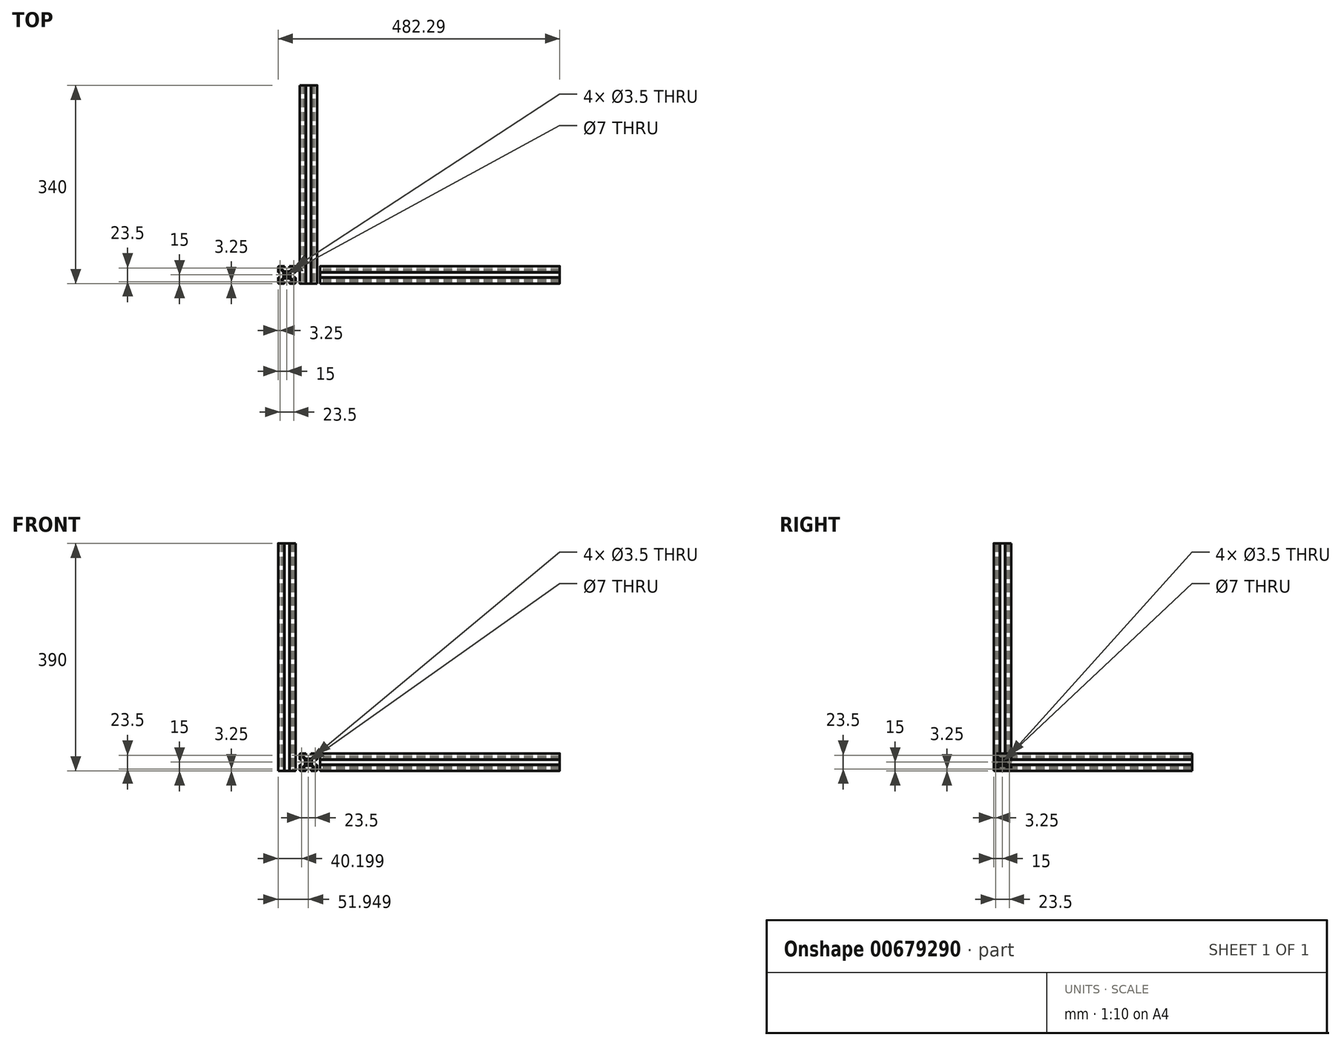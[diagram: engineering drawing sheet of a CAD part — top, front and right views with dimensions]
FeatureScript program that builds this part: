
annotation { "Feature Type Name" : "Feature", "Feature Type Description" : "" }
export const myFeature = defineFeature(function(context is Context, id is Id, definition is map)
    precondition{}
    {
        {
            var Q0;
            Q0=qCreatedBy(makeId("Front.planeOp"),FACE);
            var sketch = newSketch(context, id + "F0", { "sketchPlane" : qUnion([Q0])});
            skLineSegment(sketch, "E0.bottom", {"start": v(-33.34, 30) * mm, "end": v(-25.04, 30) * mm});
            skLineSegment(sketch, "E0.top", {"start": v(-33.34, 0) * mm, "end": v(-25.04, 0) * mm});
            skLineSegment(sketch, "E0.left", {"start": v(-35.34, 28) * mm, "end": v(-35.34, 19.7) * mm});
            skLineSegment(sketch, "E0.right", {"start": v(-5.34, 28) * mm, "end": v(-5.34, 19.7) * mm});
            skPoint(sketch, "E1", {"position": v(-20.34, 15) * mm});
            skLineSegment(sketch, "E2.bottom", {"start": v(-28.84, 27.8) * mm, "end": v(-24.44, 27.8) * mm});
            skLineSegment(sketch, "E2.left", {"start": v(-33.14, 23.5) * mm, "end": v(-33.14, 19.1) * mm});
            skCircle(sketch, "E3", {"center": v(-20.34, 15) * mm, "radius": 3.5 * mm});
            skCircle(sketch, "E4", {"center": v(-32.1, 3.25) * mm, "radius": 1.75 * mm});
            skCircle(sketch, "E5", {"center": v(-32.1, 26.75) * mm, "radius": 1.75 * mm});
            skCircle(sketch, "E6", {"center": v(-8.6, 26.75) * mm, "radius": 1.75 * mm});
            skCircle(sketch, "E7", {"center": v(-8.6, 3.25) * mm, "radius": 1.75 * mm});
            skLineSegment(sketch, "E8.right", {"start": v(-16.24, 2.2) * mm, "end": v(-16.24, 0.5) * mm});
            skLineSegment(sketch, "E9.trimOffspring", {"start": v(-16.24, 2.2) * mm, "end": v(-11.84, 2.2) * mm});
            skLineSegment(sketch, "E10.trimOffspring", {"start": v(-15.64, 0) * mm, "end": v(-7.34, 0) * mm});
            skLineSegment(sketch, "E11.trimOffspring", {"start": v(-24.44, 2.2) * mm, "end": v(-24.44, 0.5) * mm});
            skLineSegment(sketch, "E12.trimOffspring", {"start": v(-28.84, 2.2) * mm, "end": v(-24.44, 2.2) * mm});
            skLineSegment(sketch, "E13.trimOffspring", {"start": v(-7.54, 23.5) * mm, "end": v(-7.54, 19.1) * mm});
            skLineSegment(sketch, "E14", {"start": v(-24.44, 27.8) * mm, "end": v(-24.44, 29.5) * mm});
            skLineSegment(sketch, "E15", {"start": v(-16.24, 27.8) * mm, "end": v(-16.24, 29.5) * mm});
            skLineSegment(sketch, "E16.trimOffspring", {"start": v(-15.64, 30) * mm, "end": v(-7.34, 30) * mm});
            skLineSegment(sketch, "E17.trimOffspring", {"start": v(-16.24, 27.8) * mm, "end": v(-11.84, 27.8) * mm});
            skLineSegment(sketch, "E18", {"start": v(-7.54, 10.9) * mm, "end": v(-5.84, 10.9) * mm});
            skLineSegment(sketch, "E19", {"start": v(-7.54, 19.1) * mm, "end": v(-5.84, 19.1) * mm});
            skLineSegment(sketch, "E20", {"start": v(-33.14, 10.9) * mm, "end": v(-34.84, 10.9) * mm});
            skLineSegment(sketch, "E21", {"start": v(-33.14, 19.1) * mm, "end": v(-34.84, 19.1) * mm});
            skLineSegment(sketch, "E22.trimOffspring", {"start": v(-5.34, 10.3) * mm, "end": v(-5.34, 2) * mm});
            skLineSegment(sketch, "E23.trimOffspring", {"start": v(-7.54, 10.9) * mm, "end": v(-7.54, 6.5) * mm});
            skLineSegment(sketch, "E24.trimOffspring", {"start": v(-33.14, 10.9) * mm, "end": v(-33.14, 6.5) * mm});
            skLineSegment(sketch, "E25.trimOffspring", {"start": v(-35.34, 10.3) * mm, "end": v(-35.34, 2) * mm});
            skLineSegment(sketch, "E26.bottom", {"start": v(-24.93, 21) * mm, "end": v(-15.75, 21) * mm});
            skLineSegment(sketch, "E26.top", {"start": v(-24.93, 9) * mm, "end": v(-15.75, 9) * mm});
            skLineSegment(sketch, "E26.left", {"start": v(-26.34, 19.59) * mm, "end": v(-26.34, 10.41) * mm});
            skLineSegment(sketch, "E26.right", {"start": v(-14.34, 19.59) * mm, "end": v(-14.34, 10.41) * mm});
            skLineSegment(sketch, "E27", {"start": v(-28.84, 27.8) * mm, "end": v(-28.84, 24.91) * mm});
            skLineSegment(sketch, "E28", {"start": v(-30.25, 23.5) * mm, "end": v(-33.14, 23.5) * mm});
            skLineSegment(sketch, "E29", {"start": v(-11.84, 24.91) * mm, "end": v(-11.84, 27.8) * mm});
            skLineSegment(sketch, "E30", {"start": v(-10.43, 23.5) * mm, "end": v(-7.54, 23.5) * mm});
            skLineSegment(sketch, "E31", {"start": v(-10.43, 6.5) * mm, "end": v(-7.54, 6.5) * mm});
            skLineSegment(sketch, "E32", {"start": v(-11.84, 5.09) * mm, "end": v(-11.84, 2.2) * mm});
            skLineSegment(sketch, "E33", {"start": v(-28.84, 5.09) * mm, "end": v(-28.84, 2.2) * mm});
            skLineSegment(sketch, "E34", {"start": v(-30.25, 6.5) * mm, "end": v(-33.14, 6.5) * mm});
            skLineSegment(sketch, "E35", {"start": v(-30.25, 23.5) * mm, "end": v(-26.34, 19.59) * mm});
            skLineSegment(sketch, "E36", {"start": v(-28.84, 24.91) * mm, "end": v(-24.93, 21) * mm});
            skLineSegment(sketch, "E37", {"start": v(-14.34, 10.41) * mm, "end": v(-10.43, 6.5) * mm});
            skLineSegment(sketch, "E38", {"start": v(-15.75, 9) * mm, "end": v(-11.84, 5.09) * mm});
            skLineSegment(sketch, "E39", {"start": v(-28.84, 5.09) * mm, "end": v(-24.93, 9) * mm});
            skLineSegment(sketch, "E40", {"start": v(-30.25, 6.5) * mm, "end": v(-26.34, 10.41) * mm});
            skLineSegment(sketch, "E41", {"start": v(-15.75, 21) * mm, "end": v(-11.84, 24.91) * mm});
            skLineSegment(sketch, "E42", {"start": v(-14.34, 19.59) * mm, "end": v(-10.43, 23.5) * mm});
            skArc(sketch, "E43.filletArc", {"start": v(-33.34, 30) * mm, "mid": v(-34.75, 29.41) * mm, "end": v(-35.34, 28) * mm});
            skArc(sketch, "E44.filletArc", {"start": v(-5.34, 28) * mm, "mid": v(-5.93, 29.41) * mm, "end": v(-7.34, 30) * mm});
            skArc(sketch, "E45.filletArc", {"start": v(-7.34, 0) * mm, "mid": v(-5.93, 0.59) * mm, "end": v(-5.34, 2) * mm});
            skArc(sketch, "E46.filletArc", {"start": v(-35.34, 2) * mm, "mid": v(-34.75, 0.59) * mm, "end": v(-33.34, 0) * mm});
            skLineSegment(sketch, "E47", {"start": v(-5.84, 19.1) * mm, "end": v(-5.84, 19.7) * mm});
            skLineSegment(sketch, "E48", {"start": v(-5.84, 19.7) * mm, "end": v(-5.34, 19.7) * mm});
            skLineSegment(sketch, "E49.top", {"start": v(-5.34, 10.3) * mm, "end": v(-5.84, 10.3) * mm});
            skLineSegment(sketch, "E49.right", {"start": v(-5.84, 10.9) * mm, "end": v(-5.84, 10.3) * mm});
            skLineSegment(sketch, "E50.top", {"start": v(-16.24, 0.5) * mm, "end": v(-15.64, 0.5) * mm});
            skLineSegment(sketch, "E50.right", {"start": v(-15.64, 0) * mm, "end": v(-15.64, 0.5) * mm});
            skLineSegment(sketch, "E51.top", {"start": v(-24.44, 0.5) * mm, "end": v(-25.04, 0.5) * mm});
            skLineSegment(sketch, "E51.right", {"start": v(-25.04, 0) * mm, "end": v(-25.04, 0.5) * mm});
            skLineSegment(sketch, "E52.top", {"start": v(-35.34, 10.3) * mm, "end": v(-34.84, 10.3) * mm});
            skLineSegment(sketch, "E52.right", {"start": v(-34.84, 10.9) * mm, "end": v(-34.84, 10.3) * mm});
            skLineSegment(sketch, "E53.top", {"start": v(-35.34, 19.7) * mm, "end": v(-34.84, 19.7) * mm});
            skLineSegment(sketch, "E53.right", {"start": v(-34.84, 19.1) * mm, "end": v(-34.84, 19.7) * mm});
            skLineSegment(sketch, "E54.top", {"start": v(-24.44, 29.5) * mm, "end": v(-25.04, 29.5) * mm});
            skLineSegment(sketch, "E54.right", {"start": v(-25.04, 30) * mm, "end": v(-25.04, 29.5) * mm});
            skLineSegment(sketch, "E55.top", {"start": v(-16.24, 29.5) * mm, "end": v(-15.64, 29.5) * mm});
            skLineSegment(sketch, "E55.right", {"start": v(-15.64, 30) * mm, "end": v(-15.64, 29.5) * mm});
            skSolve(sketch);
        }
        {
            var Q0;
            Q0=qSketchRegion(id+"F0",true);
            extrude(context, id + "F1", {"entities" : qUnion([Q0]), "oppositeDirection" : true, "depth" : 340 * mm, "offsetDistance" : 25 * mm});
        }
        {
            var Q0;
            Q0=qCreatedBy(makeId("Top.planeOp"),FACE);
            var sketch = newSketch(context, id + "F2", { "sketchPlane" : qUnion([Q0])});
            skLineSegment(sketch, "E56.bottom", {"start": v(-70.29, 30) * mm, "end": v(-61.99, 30) * mm});
            skLineSegment(sketch, "E56.top", {"start": v(-70.29, 0) * mm, "end": v(-61.99, 0) * mm});
            skLineSegment(sketch, "E56.left", {"start": v(-72.29, 28) * mm, "end": v(-72.29, 19.7) * mm});
            skLineSegment(sketch, "E56.right", {"start": v(-42.29, 28) * mm, "end": v(-42.29, 19.7) * mm});
            skPoint(sketch, "E57", {"position": v(-57.29, 15) * mm});
            skLineSegment(sketch, "E58.bottom", {"start": v(-65.79, 27.8) * mm, "end": v(-61.39, 27.8) * mm});
            skLineSegment(sketch, "E58.left", {"start": v(-70.09, 23.5) * mm, "end": v(-70.09, 19.1) * mm});
            skCircle(sketch, "E59", {"center": v(-57.29, 15) * mm, "radius": 3.5 * mm});
            skCircle(sketch, "E60", {"center": v(-69.04, 3.25) * mm, "radius": 1.75 * mm});
            skCircle(sketch, "E61", {"center": v(-69.04, 26.75) * mm, "radius": 1.75 * mm});
            skCircle(sketch, "E62", {"center": v(-45.54, 26.75) * mm, "radius": 1.75 * mm});
            skCircle(sketch, "E63", {"center": v(-45.54, 3.25) * mm, "radius": 1.75 * mm});
            skLineSegment(sketch, "E64.right", {"start": v(-53.19, 2.2) * mm, "end": v(-53.19, 0.5) * mm});
            skLineSegment(sketch, "E65.trimOffspring", {"start": v(-53.19, 2.2) * mm, "end": v(-48.79, 2.2) * mm});
            skLineSegment(sketch, "E66.trimOffspring", {"start": v(-52.59, 0) * mm, "end": v(-44.29, 0) * mm});
            skLineSegment(sketch, "E67.trimOffspring", {"start": v(-61.39, 2.2) * mm, "end": v(-61.39, 0.5) * mm});
            skLineSegment(sketch, "E68.trimOffspring", {"start": v(-65.79, 2.2) * mm, "end": v(-61.39, 2.2) * mm});
            skLineSegment(sketch, "E69.trimOffspring", {"start": v(-44.49, 23.5) * mm, "end": v(-44.49, 19.1) * mm});
            skLineSegment(sketch, "E70", {"start": v(-61.39, 27.8) * mm, "end": v(-61.39, 29.5) * mm});
            skLineSegment(sketch, "E71", {"start": v(-53.19, 27.8) * mm, "end": v(-53.19, 29.5) * mm});
            skLineSegment(sketch, "E72.trimOffspring", {"start": v(-52.59, 30) * mm, "end": v(-44.29, 30) * mm});
            skLineSegment(sketch, "E73.trimOffspring", {"start": v(-53.19, 27.8) * mm, "end": v(-48.79, 27.8) * mm});
            skLineSegment(sketch, "E74", {"start": v(-44.49, 10.9) * mm, "end": v(-42.79, 10.9) * mm});
            skLineSegment(sketch, "E75", {"start": v(-44.49, 19.1) * mm, "end": v(-42.79, 19.1) * mm});
            skLineSegment(sketch, "E76", {"start": v(-70.09, 10.9) * mm, "end": v(-71.79, 10.9) * mm});
            skLineSegment(sketch, "E77", {"start": v(-70.09, 19.1) * mm, "end": v(-71.79, 19.1) * mm});
            skLineSegment(sketch, "E78.trimOffspring", {"start": v(-42.29, 10.3) * mm, "end": v(-42.29, 2) * mm});
            skLineSegment(sketch, "E79.trimOffspring", {"start": v(-44.49, 10.9) * mm, "end": v(-44.49, 6.5) * mm});
            skLineSegment(sketch, "E80.trimOffspring", {"start": v(-70.09, 10.9) * mm, "end": v(-70.09, 6.5) * mm});
            skLineSegment(sketch, "E81.trimOffspring", {"start": v(-72.29, 10.3) * mm, "end": v(-72.29, 2) * mm});
            skLineSegment(sketch, "E82.bottom", {"start": v(-61.88, 21) * mm, "end": v(-52.7, 21) * mm});
            skLineSegment(sketch, "E82.top", {"start": v(-61.88, 9) * mm, "end": v(-52.7, 9) * mm});
            skLineSegment(sketch, "E82.left", {"start": v(-63.29, 19.59) * mm, "end": v(-63.29, 10.41) * mm});
            skLineSegment(sketch, "E82.right", {"start": v(-51.29, 19.59) * mm, "end": v(-51.29, 10.41) * mm});
            skLineSegment(sketch, "E83", {"start": v(-65.79, 27.8) * mm, "end": v(-65.79, 24.91) * mm});
            skLineSegment(sketch, "E84", {"start": v(-67.2, 23.5) * mm, "end": v(-70.09, 23.5) * mm});
            skLineSegment(sketch, "E85", {"start": v(-48.79, 24.91) * mm, "end": v(-48.79, 27.8) * mm});
            skLineSegment(sketch, "E86", {"start": v(-47.38, 23.5) * mm, "end": v(-44.49, 23.5) * mm});
            skLineSegment(sketch, "E87", {"start": v(-47.38, 6.5) * mm, "end": v(-44.49, 6.5) * mm});
            skLineSegment(sketch, "E88", {"start": v(-48.79, 5.09) * mm, "end": v(-48.79, 2.2) * mm});
            skLineSegment(sketch, "E89", {"start": v(-65.79, 5.09) * mm, "end": v(-65.79, 2.2) * mm});
            skLineSegment(sketch, "E90", {"start": v(-67.2, 6.5) * mm, "end": v(-70.09, 6.5) * mm});
            skLineSegment(sketch, "E91", {"start": v(-67.2, 23.5) * mm, "end": v(-63.29, 19.59) * mm});
            skLineSegment(sketch, "E92", {"start": v(-65.79, 24.91) * mm, "end": v(-61.88, 21) * mm});
            skLineSegment(sketch, "E93", {"start": v(-51.29, 10.41) * mm, "end": v(-47.38, 6.5) * mm});
            skLineSegment(sketch, "E94", {"start": v(-52.7, 9) * mm, "end": v(-48.79, 5.09) * mm});
            skLineSegment(sketch, "E95", {"start": v(-65.79, 5.09) * mm, "end": v(-61.88, 9) * mm});
            skLineSegment(sketch, "E96", {"start": v(-67.2, 6.5) * mm, "end": v(-63.29, 10.41) * mm});
            skLineSegment(sketch, "E97", {"start": v(-52.7, 21) * mm, "end": v(-48.79, 24.91) * mm});
            skLineSegment(sketch, "E98", {"start": v(-51.29, 19.59) * mm, "end": v(-47.38, 23.5) * mm});
            skArc(sketch, "E99.filletArc", {"start": v(-70.29, 30) * mm, "mid": v(-71.7, 29.41) * mm, "end": v(-72.29, 28) * mm});
            skArc(sketch, "E100.filletArc", {"start": v(-42.29, 28) * mm, "mid": v(-42.88, 29.41) * mm, "end": v(-44.29, 30) * mm});
            skArc(sketch, "E101.filletArc", {"start": v(-44.29, 0) * mm, "mid": v(-42.88, 0.59) * mm, "end": v(-42.29, 2) * mm});
            skArc(sketch, "E102.filletArc", {"start": v(-72.29, 2) * mm, "mid": v(-71.7, 0.59) * mm, "end": v(-70.29, 0) * mm});
            skLineSegment(sketch, "E103", {"start": v(-42.79, 19.1) * mm, "end": v(-42.79, 19.7) * mm});
            skLineSegment(sketch, "E104", {"start": v(-42.79, 19.7) * mm, "end": v(-42.29, 19.7) * mm});
            skLineSegment(sketch, "E105.top", {"start": v(-42.29, 10.3) * mm, "end": v(-42.79, 10.3) * mm});
            skLineSegment(sketch, "E105.right", {"start": v(-42.79, 10.9) * mm, "end": v(-42.79, 10.3) * mm});
            skLineSegment(sketch, "E106.top", {"start": v(-53.19, 0.5) * mm, "end": v(-52.59, 0.5) * mm});
            skLineSegment(sketch, "E106.right", {"start": v(-52.59, 0) * mm, "end": v(-52.59, 0.5) * mm});
            skLineSegment(sketch, "E107.top", {"start": v(-61.39, 0.5) * mm, "end": v(-61.99, 0.5) * mm});
            skLineSegment(sketch, "E107.right", {"start": v(-61.99, 0) * mm, "end": v(-61.99, 0.5) * mm});
            skLineSegment(sketch, "E108.top", {"start": v(-72.29, 10.3) * mm, "end": v(-71.79, 10.3) * mm});
            skLineSegment(sketch, "E108.right", {"start": v(-71.79, 10.9) * mm, "end": v(-71.79, 10.3) * mm});
            skLineSegment(sketch, "E109.top", {"start": v(-72.29, 19.7) * mm, "end": v(-71.79, 19.7) * mm});
            skLineSegment(sketch, "E109.right", {"start": v(-71.79, 19.1) * mm, "end": v(-71.79, 19.7) * mm});
            skLineSegment(sketch, "E110.top", {"start": v(-61.39, 29.5) * mm, "end": v(-61.99, 29.5) * mm});
            skLineSegment(sketch, "E110.right", {"start": v(-61.99, 30) * mm, "end": v(-61.99, 29.5) * mm});
            skLineSegment(sketch, "E111.top", {"start": v(-53.19, 29.5) * mm, "end": v(-52.59, 29.5) * mm});
            skLineSegment(sketch, "E111.right", {"start": v(-52.59, 30) * mm, "end": v(-52.59, 29.5) * mm});
            skSolve(sketch);
        }
        {
            var Q0;
            Q0=qSketchRegion(id+"F2",true);
            extrude(context, id + "F3", {"entities" : qUnion([Q0]), "depth" : 390 * mm, "offsetDistance" : 25 * mm});
        }
        {
            var Q0;
            Q0=qCreatedBy(makeId("Right.planeOp"),FACE);
            var sketch = newSketch(context, id + "F4", { "sketchPlane" : qUnion([Q0])});
            skLineSegment(sketch, "E112.bottom", {"start": v(2, 30) * mm, "end": v(10.3, 30) * mm});
            skLineSegment(sketch, "E112.top", {"start": v(2, 0) * mm, "end": v(10.3, 0) * mm});
            skLineSegment(sketch, "E112.left", {"start": v(0, 28) * mm, "end": v(0, 19.7) * mm});
            skLineSegment(sketch, "E112.right", {"start": v(30, 28) * mm, "end": v(30, 19.7) * mm});
            skPoint(sketch, "E113", {"position": v(15, 15) * mm});
            skLineSegment(sketch, "E114.bottom", {"start": v(6.5, 27.8) * mm, "end": v(10.9, 27.8) * mm});
            skLineSegment(sketch, "E114.left", {"start": v(2.2, 23.5) * mm, "end": v(2.2, 19.1) * mm});
            skCircle(sketch, "E115", {"center": v(15, 15) * mm, "radius": 3.5 * mm});
            skCircle(sketch, "E116", {"center": v(3.25, 3.25) * mm, "radius": 1.75 * mm});
            skCircle(sketch, "E117", {"center": v(3.25, 26.75) * mm, "radius": 1.75 * mm});
            skCircle(sketch, "E118", {"center": v(26.75, 26.75) * mm, "radius": 1.75 * mm});
            skCircle(sketch, "E119", {"center": v(26.75, 3.25) * mm, "radius": 1.75 * mm});
            skLineSegment(sketch, "E120.right", {"start": v(19.1, 2.2) * mm, "end": v(19.1, 0.5) * mm});
            skLineSegment(sketch, "E121.trimOffspring", {"start": v(19.1, 2.2) * mm, "end": v(23.5, 2.2) * mm});
            skLineSegment(sketch, "E122.trimOffspring", {"start": v(19.7, 0) * mm, "end": v(28, 0) * mm});
            skLineSegment(sketch, "E123.trimOffspring", {"start": v(10.9, 2.2) * mm, "end": v(10.9, 0.5) * mm});
            skLineSegment(sketch, "E124.trimOffspring", {"start": v(6.5, 2.2) * mm, "end": v(10.9, 2.2) * mm});
            skLineSegment(sketch, "E125.trimOffspring", {"start": v(27.8, 23.5) * mm, "end": v(27.8, 19.1) * mm});
            skLineSegment(sketch, "E126", {"start": v(10.9, 27.8) * mm, "end": v(10.9, 29.5) * mm});
            skLineSegment(sketch, "E127", {"start": v(19.1, 27.8) * mm, "end": v(19.1, 29.5) * mm});
            skLineSegment(sketch, "E128.trimOffspring", {"start": v(19.7, 30) * mm, "end": v(28, 30) * mm});
            skLineSegment(sketch, "E129.trimOffspring", {"start": v(19.1, 27.8) * mm, "end": v(23.5, 27.8) * mm});
            skLineSegment(sketch, "E130", {"start": v(27.8, 10.9) * mm, "end": v(29.5, 10.9) * mm});
            skLineSegment(sketch, "E131", {"start": v(27.8, 19.1) * mm, "end": v(29.5, 19.1) * mm});
            skLineSegment(sketch, "E132", {"start": v(2.2, 10.9) * mm, "end": v(0.5, 10.9) * mm});
            skLineSegment(sketch, "E133", {"start": v(2.2, 19.1) * mm, "end": v(0.5, 19.1) * mm});
            skLineSegment(sketch, "E134.trimOffspring", {"start": v(30, 10.3) * mm, "end": v(30, 2) * mm});
            skLineSegment(sketch, "E135.trimOffspring", {"start": v(27.8, 10.9) * mm, "end": v(27.8, 6.5) * mm});
            skLineSegment(sketch, "E136.trimOffspring", {"start": v(2.2, 10.9) * mm, "end": v(2.2, 6.5) * mm});
            skLineSegment(sketch, "E137.trimOffspring", {"start": v(0, 10.3) * mm, "end": v(0, 2) * mm});
            skLineSegment(sketch, "E138.bottom", {"start": v(10.41, 21) * mm, "end": v(19.59, 21) * mm});
            skLineSegment(sketch, "E138.top", {"start": v(10.41, 9) * mm, "end": v(19.59, 9) * mm});
            skLineSegment(sketch, "E138.left", {"start": v(9, 19.59) * mm, "end": v(9, 10.41) * mm});
            skLineSegment(sketch, "E138.right", {"start": v(21, 19.59) * mm, "end": v(21, 10.41) * mm});
            skLineSegment(sketch, "E139", {"start": v(6.5, 27.8) * mm, "end": v(6.5, 24.91) * mm});
            skLineSegment(sketch, "E140", {"start": v(5.09, 23.5) * mm, "end": v(2.2, 23.5) * mm});
            skLineSegment(sketch, "E141", {"start": v(23.5, 24.91) * mm, "end": v(23.5, 27.8) * mm});
            skLineSegment(sketch, "E142", {"start": v(24.91, 23.5) * mm, "end": v(27.8, 23.5) * mm});
            skLineSegment(sketch, "E143", {"start": v(24.91, 6.5) * mm, "end": v(27.8, 6.5) * mm});
            skLineSegment(sketch, "E144", {"start": v(23.5, 5.09) * mm, "end": v(23.5, 2.2) * mm});
            skLineSegment(sketch, "E145", {"start": v(6.5, 5.09) * mm, "end": v(6.5, 2.2) * mm});
            skLineSegment(sketch, "E146", {"start": v(5.09, 6.5) * mm, "end": v(2.2, 6.5) * mm});
            skLineSegment(sketch, "E147", {"start": v(5.09, 23.5) * mm, "end": v(9, 19.59) * mm});
            skLineSegment(sketch, "E148", {"start": v(6.5, 24.91) * mm, "end": v(10.41, 21) * mm});
            skLineSegment(sketch, "E149", {"start": v(21, 10.41) * mm, "end": v(24.91, 6.5) * mm});
            skLineSegment(sketch, "E150", {"start": v(19.59, 9) * mm, "end": v(23.5, 5.09) * mm});
            skLineSegment(sketch, "E151", {"start": v(6.5, 5.09) * mm, "end": v(10.41, 9) * mm});
            skLineSegment(sketch, "E152", {"start": v(5.09, 6.5) * mm, "end": v(9, 10.41) * mm});
            skLineSegment(sketch, "E153", {"start": v(19.59, 21) * mm, "end": v(23.5, 24.91) * mm});
            skLineSegment(sketch, "E154", {"start": v(21, 19.59) * mm, "end": v(24.91, 23.5) * mm});
            skArc(sketch, "E155.filletArc", {"start": v(2, 30) * mm, "mid": v(0.59, 29.41) * mm, "end": v(0, 28) * mm});
            skArc(sketch, "E156.filletArc", {"start": v(30, 28) * mm, "mid": v(29.41, 29.41) * mm, "end": v(28, 30) * mm});
            skArc(sketch, "E157.filletArc", {"start": v(28, 0) * mm, "mid": v(29.41, 0.59) * mm, "end": v(30, 2) * mm});
            skArc(sketch, "E158.filletArc", {"start": v(0, 2) * mm, "mid": v(0.59, 0.59) * mm, "end": v(2, 0) * mm});
            skLineSegment(sketch, "E159", {"start": v(29.5, 19.1) * mm, "end": v(29.5, 19.7) * mm});
            skLineSegment(sketch, "E160", {"start": v(29.5, 19.7) * mm, "end": v(30, 19.7) * mm});
            skLineSegment(sketch, "E161.top", {"start": v(30, 10.3) * mm, "end": v(29.5, 10.3) * mm});
            skLineSegment(sketch, "E161.right", {"start": v(29.5, 10.9) * mm, "end": v(29.5, 10.3) * mm});
            skLineSegment(sketch, "E162.top", {"start": v(19.1, 0.5) * mm, "end": v(19.7, 0.5) * mm});
            skLineSegment(sketch, "E162.right", {"start": v(19.7, 0) * mm, "end": v(19.7, 0.5) * mm});
            skLineSegment(sketch, "E163.top", {"start": v(10.9, 0.5) * mm, "end": v(10.3, 0.5) * mm});
            skLineSegment(sketch, "E163.right", {"start": v(10.3, 0) * mm, "end": v(10.3, 0.5) * mm});
            skLineSegment(sketch, "E164.top", {"start": v(0, 10.3) * mm, "end": v(0.5, 10.3) * mm});
            skLineSegment(sketch, "E164.right", {"start": v(0.5, 10.9) * mm, "end": v(0.5, 10.3) * mm});
            skLineSegment(sketch, "E165.top", {"start": v(0, 19.7) * mm, "end": v(0.5, 19.7) * mm});
            skLineSegment(sketch, "E165.right", {"start": v(0.5, 19.1) * mm, "end": v(0.5, 19.7) * mm});
            skLineSegment(sketch, "E166.top", {"start": v(10.9, 29.5) * mm, "end": v(10.3, 29.5) * mm});
            skLineSegment(sketch, "E166.right", {"start": v(10.3, 30) * mm, "end": v(10.3, 29.5) * mm});
            skLineSegment(sketch, "E167.top", {"start": v(19.1, 29.5) * mm, "end": v(19.7, 29.5) * mm});
            skLineSegment(sketch, "E167.right", {"start": v(19.7, 30) * mm, "end": v(19.7, 29.5) * mm});
            skSolve(sketch);
        }
        {
            var Q0;
            Q0=qSketchRegion(id+"F4",true);
            extrude(context, id + "F5", {"entities" : qUnion([Q0]), "depth" : 410 * mm, "offsetDistance" : 25 * mm});
        }
    });
